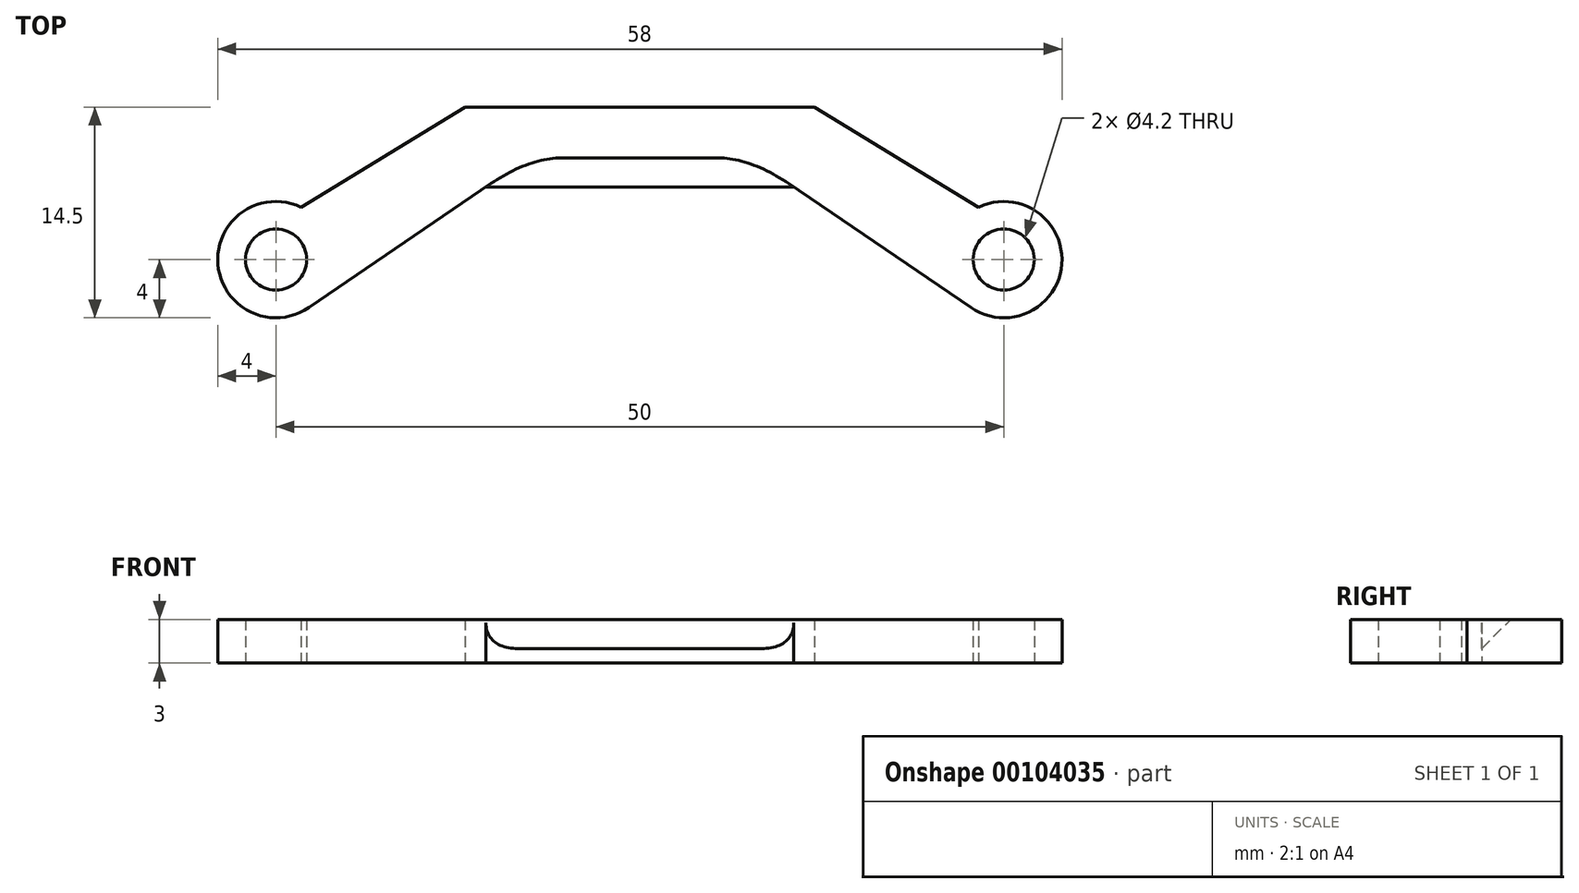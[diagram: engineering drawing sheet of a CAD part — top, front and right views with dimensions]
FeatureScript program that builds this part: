
annotation { "Feature Type Name" : "Feature", "Feature Type Description" : "" }
export const myFeature = defineFeature(function(context is Context, id is Id, definition is map)
    precondition{}
    {
        {
            var Q0;
            Q0=qCreatedBy(makeId("Top.planeOp"),FACE);
            var sketch = newSketch(context, id + "F0", { "sketchPlane" : qUnion([Q0])});
            skLineSegment(sketch, "E0", {"start": v(0, 14.5) * mm, "end": v(-12, 14.5) * mm});
            skLineSegment(sketch, "E1", {"start": v(-12, 14.5) * mm, "end": v(-23.27, 7.6) * mm});
            skLineSegment(sketch, "E2", {"start": v(0, 9) * mm, "end": v(-10.57, 9) * mm});
            skLineSegment(sketch, "E3", {"start": v(-10.57, 9) * mm, "end": v(-22.75, 0.7) * mm});
            skArc(sketch, "E4", {"start": v(-23.27, 7.6) * mm, "mid": v(-28.99, 3.7) * mm, "end": v(-22.75, 0.7) * mm});
            skLineSegment(sketch, "E5", {"start": v(0, 14.5) * mm, "end": v(0, 9) * mm});
            skCircle(sketch, "E6", {"center": v(-25, 4) * mm, "radius": 2.1 * mm});
            skSolve(sketch);
        }
        {
            var Q0;
            Q0=makeQuery(id+"F0.imprint","IMPRINT",FACE,{"disambiguationData":[TD([[makeQuery(id+"F0.imprint","IMPRINT",EDGE,{"derivedFrom":sQuery(id+"F0.wireOp",EDGE,"E0")}),1.0]])]});
            extrude(context, id + "F1", {"entities" : qUnion([Q0]), "depth" : 3 * mm});
        }
        {
            var Q0;
            Q0=makeQuery(id+"F1.opExtrude","SWEPT_BODY",BODY,{"disambiguationData":[OSD([sQuery(id+"F0.wireOp",EDGE,"E0"),sQuery(id+"F0.wireOp",EDGE,"E1"),sQuery(id+"F0.wireOp",EDGE,"E2"),sQuery(id+"F0.wireOp",EDGE,"E3"),sQuery(id+"F0.wireOp",EDGE,"E4"),sQuery(id+"F0.wireOp",EDGE,"E5"),sQuery(id+"F0.wireOp",EDGE,"E6")])]});
            var Q1;
            Q1=qCreatedBy(makeId("Right.planeOp"),FACE);
            mirror(context, id + "F2", {"operationType" : NewBodyOperationType.ADD, "entities" : qUnion([Q0]), "mirrorPlane" : qUnion([Q1])});
        }
        {
            var Q0;
            {var subQ0=makeQuery(id+"F1.opExtrude","CAP_EDGE",EDGE,{"disambiguationData":[OSD([sQuery(id+"F0.wireOp",EDGE,"E2")])],"isStart":false});Q0=makeQuery(id+"F2.boolean.opBoolean","MERGE",EDGE,{"derivedFrom":[subQ0,makeQuery(id+"F2.opPattern","COPY",EDGE,{"derivedFrom":subQ0,"instanceName":"1"})]});}
            chamfer(context, id + "F3", {"entities" : qUnion([Q0]), "chamferType" : ChamferType.TWO_OFFSETS, "width1" : 2 * mm, "oppositeDirection" : false, "width2" : 2 * mm, "tangentPropagation" : true});
        }
        {
            var Q0;
            {var subQ0=makeQuery(id+"F1.opExtrude","CAP_EDGE",EDGE,{"disambiguationData":[OSD([sQuery(id+"F0.wireOp",EDGE,"E2")])],"isStart":false});Q0=makeQuery(id+"F3.opChamfer","BLEND_EDGE",EDGE,{"blendedFrom":[makeQuery(id+"F2.boolean.opBoolean","MERGE",EDGE,{"derivedFrom":[subQ0,makeQuery(id+"F2.opPattern","COPY",EDGE,{"derivedFrom":subQ0,"instanceName":"1"})]}),makeQuery(id+"F2.opPattern","COPY",FACE,{"derivedFrom":makeQuery(id+"F1.opExtrude","SWEPT_FACE",FACE,{"disambiguationData":[OSD([sQuery(id+"F0.wireOp",EDGE,"E3")])]}),"instanceName":"1"})],"blendedInto":[makeQuery(id+"F2.opPattern","COPY",FACE,{"derivedFrom":makeQuery(id+"F1.opExtrude","SWEPT_FACE",FACE,{"disambiguationData":[OSD([sQuery(id+"F0.wireOp",EDGE,"E3")])]}),"instanceName":"1"})]});}
            var Q1;
            {var subQ0=makeQuery(id+"F1.opExtrude","CAP_EDGE",EDGE,{"disambiguationData":[OSD([sQuery(id+"F0.wireOp",EDGE,"E2")])],"isStart":false});Q1=makeQuery(id+"F3.opChamfer","BLEND_EDGE",EDGE,{"blendedFrom":[makeQuery(id+"F2.boolean.opBoolean","MERGE",EDGE,{"derivedFrom":[subQ0,makeQuery(id+"F2.opPattern","COPY",EDGE,{"derivedFrom":subQ0,"instanceName":"1"})]}),makeQuery(id+"F1.opExtrude","SWEPT_FACE",FACE,{"disambiguationData":[OSD([sQuery(id+"F0.wireOp",EDGE,"E3")])]})],"blendedInto":[makeQuery(id+"F1.opExtrude","SWEPT_FACE",FACE,{"disambiguationData":[OSD([sQuery(id+"F0.wireOp",EDGE,"E3")])]})]});}
            fillet(context, id + "F4", {"entities" : qUnion([Q0, Q1]), "radius" : 3 * mm, "tangentPropagation" : true, "allowEdgeOverflow" : false});
        }
    });
